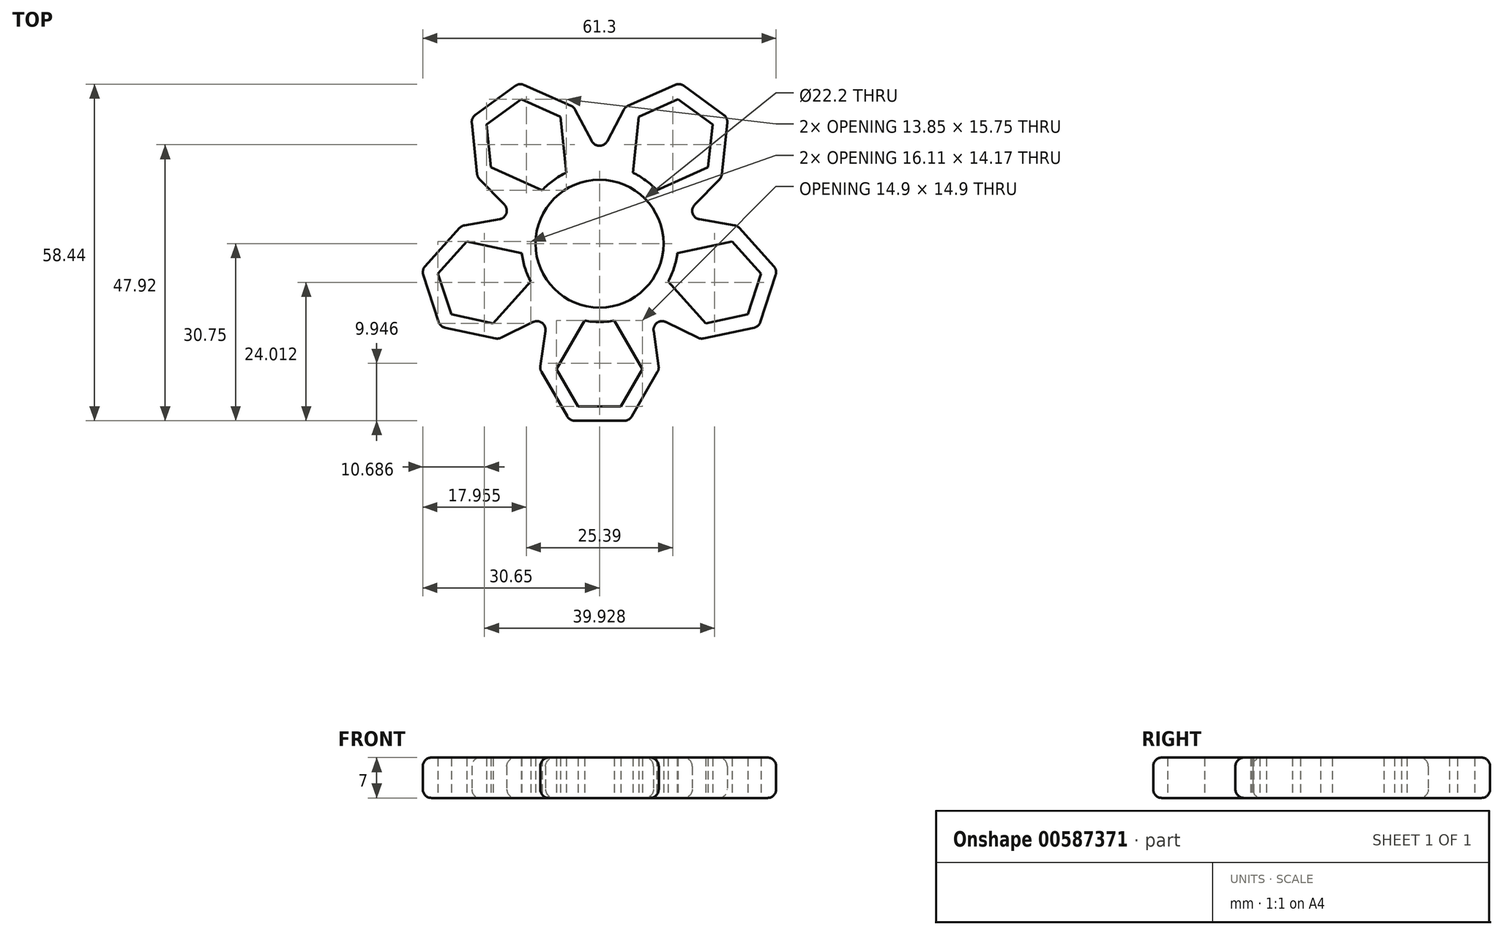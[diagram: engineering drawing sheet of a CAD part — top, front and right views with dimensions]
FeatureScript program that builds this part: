
annotation { "Feature Type Name" : "Feature", "Feature Type Description" : "" }
export const myFeature = defineFeature(function(context is Context, id is Id, definition is map)
    precondition{}
    {
        {
            var Q0;
            Q0=qCreatedBy(makeId("Top.planeOp"),FACE);
            var sketch = newSketch(context, id + "F0", { "sketchPlane" : qUnion([Q0])});
            skCircle(sketch, "E0", {"center": v(0, 0) * mm, "radius": 11.1 * mm});
            skCircle(sketch, "E1.0", {"center": v(0, 0) * mm, "radius": 13.6 * mm});
            skCircle(sketch, "E2.cCircle", {"center": v(0, -21.8) * mm, "radius": 6.45 * mm, "construction": true});
            skLineSegment(sketch, "E2.0", {"start": v(3.72, -28.25) * mm, "end": v(-3.72, -28.25) * mm});
            skLineSegment(sketch, "E2.1", {"start": v(-3.72, -28.25) * mm, "end": v(-7.45, -21.8) * mm});
            skLineSegment(sketch, "E2.2", {"start": v(-7.45, -21.8) * mm, "end": v(-2.96, -14.04) * mm});
            skLineSegment(sketch, "E2.4", {"start": v(3.72, -15.35) * mm, "end": v(7.45, -21.8) * mm});
            skLineSegment(sketch, "E2.5", {"start": v(7.45, -21.8) * mm, "end": v(3.72, -28.25) * mm});
            skPoint(sketch, "E2.0.midPoint", {"position": v(0, -28.25) * mm});
            skLineSegment(sketch, "E3.2", {"start": v(10.33, -21.8) * mm, "end": v(5.17, -30.75) * mm});
            skLineSegment(sketch, "E3.3", {"start": v(5.17, -30.75) * mm, "end": v(-5.17, -30.75) * mm});
            skLineSegment(sketch, "E3.4", {"start": v(-5.17, -30.75) * mm, "end": v(-10.33, -21.8) * mm});
            skLineSegment(sketch, "E4", {"start": v(-10.33, -21.8) * mm, "end": v(-8.7, -10.45) * mm});
            skLineSegment(sketch, "E5", {"start": v(10.33, -21.8) * mm, "end": v(8.7, -10.45) * mm});
            skFitSpline(sketch, "E6", {"points": [v(-8.7, -10.45) * mm, v(8.7, -10.45) * mm], "startDerivative": vector(17.15, -3.94) * mm, "endDerivative": vector(17.1, 4.44) * mm});
            skLineSegment(sketch, "E7", {"start": v(-2.96, -14.04) * mm, "end": v(-2.57, -13.35) * mm});
            skLineSegment(sketch, "E8", {"start": v(3.72, -15.35) * mm, "end": v(2.57, -13.35) * mm});
            skLineSegment(sketch, "E9.1.0", {"start": v(23.93, 3.1) * mm, "end": v(12.63, 5.05) * mm});
            skLineSegment(sketch, "E9.1.1", {"start": v(15.75, -1.2) * mm, "end": v(23.04, 0.35) * mm});
            skLineSegment(sketch, "E9.1.2", {"start": v(23.93, 3.1) * mm, "end": v(30.84, -4.59) * mm});
            skLineSegment(sketch, "E9.1.3", {"start": v(28.02, -5.19) * mm, "end": v(25.72, -12.27) * mm});
            skLineSegment(sketch, "E9.1.4", {"start": v(30.84, -4.59) * mm, "end": v(27.65, -14.42) * mm});
            skPoint(sketch, "E9.1.5", {"position": v(26.87, -8.73) * mm});
            skLineSegment(sketch, "E9.1.6", {"start": v(27.65, -14.42) * mm, "end": v(17.54, -16.57) * mm});
            skLineSegment(sketch, "E9.1.7", {"start": v(17.54, -16.57) * mm, "end": v(7.25, -11.5) * mm});
            skLineSegment(sketch, "E9.1.8", {"start": v(25.72, -12.27) * mm, "end": v(18.43, -13.82) * mm});
            skLineSegment(sketch, "E9.1.9", {"start": v(23.04, 0.35) * mm, "end": v(28.02, -5.19) * mm});
            skLineSegment(sketch, "E9.1.10", {"start": v(15.75, -1.2) * mm, "end": v(13.5, -1.68) * mm});
            skLineSegment(sketch, "E9.1.11", {"start": v(18.43, -13.82) * mm, "end": v(12.43, -7.16) * mm});
            skCircle(sketch, "E9.1.12", {"center": v(20.74, -6.74) * mm, "radius": 6.45 * mm, "construction": true});
            skLineSegment(sketch, "E9.1.13", {"start": v(12.43, -7.16) * mm, "end": v(11.9, -6.57) * mm});
            skLineSegment(sketch, "E9.2.0", {"start": v(4.45, 23.71) * mm, "end": v(-0.9, 13.57) * mm});
            skLineSegment(sketch, "E9.2.1", {"start": v(6.01, 14.6) * mm, "end": v(6.8, 22.02) * mm});
            skLineSegment(sketch, "E9.2.2", {"start": v(4.45, 23.71) * mm, "end": v(13.9, 27.92) * mm});
            skLineSegment(sketch, "E9.2.3", {"start": v(13.6, 25.05) * mm, "end": v(19.62, 20.67) * mm});
            skLineSegment(sketch, "E9.2.4", {"start": v(13.9, 27.92) * mm, "end": v(22.26, 21.84) * mm});
            skPoint(sketch, "E9.2.5", {"position": v(16.6, 22.86) * mm});
            skLineSegment(sketch, "E9.2.6", {"start": v(22.26, 21.84) * mm, "end": v(21.18, 11.56) * mm});
            skLineSegment(sketch, "E9.2.7", {"start": v(21.18, 11.56) * mm, "end": v(13.18, 3.34) * mm});
            skLineSegment(sketch, "E9.2.8", {"start": v(19.62, 20.67) * mm, "end": v(18.84, 13.26) * mm});
            skLineSegment(sketch, "E9.2.9", {"start": v(6.8, 22.02) * mm, "end": v(13.6, 25.05) * mm});
            skLineSegment(sketch, "E9.2.10", {"start": v(6.01, 14.6) * mm, "end": v(5.77, 12.32) * mm});
            skLineSegment(sketch, "E9.2.11", {"start": v(18.84, 13.26) * mm, "end": v(10.65, 9.61) * mm});
            skCircle(sketch, "E9.2.12", {"center": v(12.82, 17.64) * mm, "radius": 6.45 * mm, "construction": true});
            skLineSegment(sketch, "E9.2.13", {"start": v(10.65, 9.61) * mm, "end": v(9.93, 9.3) * mm});
            skLineSegment(sketch, "E9.3.0", {"start": v(-21.18, 11.56) * mm, "end": v(-13.19, 3.33) * mm});
            skLineSegment(sketch, "E9.3.1", {"start": v(-12.04, 10.23) * mm, "end": v(-18.84, 13.26) * mm});
            skLineSegment(sketch, "E9.3.2", {"start": v(-21.18, 11.56) * mm, "end": v(-22.26, 21.84) * mm});
            skLineSegment(sketch, "E9.3.3", {"start": v(-19.62, 20.67) * mm, "end": v(-13.6, 25.05) * mm});
            skLineSegment(sketch, "E9.3.4", {"start": v(-22.26, 21.84) * mm, "end": v(-13.9, 27.92) * mm});
            skPoint(sketch, "E9.3.5", {"position": v(-16.6, 22.86) * mm});
            skLineSegment(sketch, "E9.3.6", {"start": v(-13.9, 27.92) * mm, "end": v(-4.45, 23.71) * mm});
            skLineSegment(sketch, "E9.3.7", {"start": v(-4.45, 23.71) * mm, "end": v(0.9, 13.57) * mm});
            skLineSegment(sketch, "E9.3.8", {"start": v(-13.6, 25.05) * mm, "end": v(-6.8, 22.02) * mm});
            skLineSegment(sketch, "E9.3.9", {"start": v(-18.84, 13.26) * mm, "end": v(-19.62, 20.67) * mm});
            skLineSegment(sketch, "E9.3.10", {"start": v(-12.04, 10.23) * mm, "end": v(-9.93, 9.3) * mm});
            skLineSegment(sketch, "E9.3.11", {"start": v(-6.8, 22.02) * mm, "end": v(-5.85, 13.1) * mm});
            skCircle(sketch, "E9.3.12", {"center": v(-12.82, 17.64) * mm, "radius": 6.45 * mm, "construction": true});
            skLineSegment(sketch, "E9.3.13", {"start": v(-5.85, 13.1) * mm, "end": v(-5.77, 12.32) * mm});
            skLineSegment(sketch, "E9.4.0", {"start": v(-17.54, -16.57) * mm, "end": v(-7.24, -11.51) * mm});
            skLineSegment(sketch, "E9.4.1", {"start": v(-13.45, -8.29) * mm, "end": v(-18.43, -13.82) * mm});
            skLineSegment(sketch, "E9.4.2", {"start": v(-17.54, -16.57) * mm, "end": v(-27.65, -14.42) * mm});
            skLineSegment(sketch, "E9.4.3", {"start": v(-25.72, -12.27) * mm, "end": v(-28.02, -5.19) * mm});
            skLineSegment(sketch, "E9.4.4", {"start": v(-27.65, -14.42) * mm, "end": v(-30.84, -4.59) * mm});
            skPoint(sketch, "E9.4.5", {"position": v(-26.87, -8.73) * mm});
            skLineSegment(sketch, "E9.4.6", {"start": v(-30.84, -4.59) * mm, "end": v(-23.93, 3.1) * mm});
            skLineSegment(sketch, "E9.4.7", {"start": v(-23.93, 3.1) * mm, "end": v(-12.62, 5.05) * mm});
            skLineSegment(sketch, "E9.4.8", {"start": v(-28.02, -5.19) * mm, "end": v(-23.04, 0.35) * mm});
            skLineSegment(sketch, "E9.4.9", {"start": v(-18.43, -13.82) * mm, "end": v(-25.72, -12.27) * mm});
            skLineSegment(sketch, "E9.4.10", {"start": v(-13.45, -8.29) * mm, "end": v(-11.9, -6.57) * mm});
            skLineSegment(sketch, "E9.4.11", {"start": v(-23.04, 0.35) * mm, "end": v(-14.27, -1.52) * mm});
            skCircle(sketch, "E9.4.12", {"center": v(-20.74, -6.74) * mm, "radius": 6.45 * mm, "construction": true});
            skLineSegment(sketch, "E9.4.13", {"start": v(-14.27, -1.52) * mm, "end": v(-13.5, -1.68) * mm});
            skSolve(sketch);
        }
        {
            var Q0;
            Q0=makeQuery(id+"F0.imprint","IMPRINT",FACE,{"disambiguationData":[TD([[makeQuery(id+"F0.imprint","IMPRINT",EDGE,{"derivedFrom":sQuery(id+"F0.wireOp",EDGE,"E0")}),-1.0]])]});
            var Q1;
            {var subQ4=sQuery(id+"F0.wireOp",EDGE,"E6");Q1=makeQuery(id+"F0.imprint","IMPRINT",FACE,{"disambiguationData":[TD([[makeQuery(id+"F0.imprint","IMPRINT",EDGE,{"derivedFrom":subQ4}),-1.0]])]});}
            extrude(context, id + "F1", {"entities" : qUnion([Q0, Q1]), "endBound" : BoundingType.SYMMETRIC, "depth" : 7 * mm, "offsetDistance" : 25 * mm});
        }
        {
            var Q0;
            Q0=makeQuery(id+"F0.imprint","IMPRINT",FACE,{"disambiguationData":[TD([[makeQuery(id+"F0.imprint","IMPRINT",EDGE,{"derivedFrom":sQuery(id+"F0.wireOp",EDGE,"E2.0")}),1.0]])]});
            var Q1;
            {var subQ4=sQuery(id+"F0.wireOp",EDGE,"E6");Q1=makeQuery(id+"F0.imprint","IMPRINT",FACE,{"disambiguationData":[TD([[makeQuery(id+"F0.imprint","IMPRINT",EDGE,{"derivedFrom":subQ4}),-1.0]])]});}
            var Q2;
            {var subQ0=sQuery(id+"F0.wireOp",EDGE,"E9.4.0");var subQ1=sQuery(id+"F0.wireOp",EDGE,"E1.0");var subQ2=makeQuery(id+"F0.imprint","INTERSECT",VERTEX,{"derivedFrom":[subQ1,subQ0]});Q2=makeQuery(id+"F0.imprint","IMPRINT",FACE,{"disambiguationData":[TD([[makeQuery(id+"F0.imprint","IMPRINT",EDGE,{"disambiguationData":[TD([[subQ2,1.0]])],"derivedFrom":subQ1}),-1.0]])]});}
            var Q3;
            Q3=makeQuery(id+"F0.imprint","IMPRINT",FACE,{"disambiguationData":[TD([[makeQuery(id+"F0.imprint","IMPRINT",EDGE,{"derivedFrom":sQuery(id+"F0.wireOp",EDGE,"E9.4.1")}),1.0]])]});
            var Q4;
            {var subQ0=sQuery(id+"F0.wireOp",EDGE,"E9.3.0");var subQ1=sQuery(id+"F0.wireOp",EDGE,"E1.0");var subQ2=makeQuery(id+"F0.imprint","INTERSECT",VERTEX,{"derivedFrom":[subQ1,subQ0]});Q4=makeQuery(id+"F0.imprint","IMPRINT",FACE,{"disambiguationData":[TD([[makeQuery(id+"F0.imprint","IMPRINT",EDGE,{"disambiguationData":[TD([[subQ2,1.0]])],"derivedFrom":subQ1}),-1.0]])]});}
            var Q5;
            Q5=makeQuery(id+"F0.imprint","IMPRINT",FACE,{"disambiguationData":[TD([[makeQuery(id+"F0.imprint","IMPRINT",EDGE,{"derivedFrom":sQuery(id+"F0.wireOp",EDGE,"E9.3.1")}),1.0]])]});
            var Q6;
            {var subQ0=sQuery(id+"F0.wireOp",EDGE,"E9.1.0");var subQ1=sQuery(id+"F0.wireOp",EDGE,"E1.0");var subQ2=makeQuery(id+"F0.imprint","INTERSECT",VERTEX,{"derivedFrom":[subQ1,subQ0]});Q6=makeQuery(id+"F0.imprint","IMPRINT",FACE,{"disambiguationData":[TD([[makeQuery(id+"F0.imprint","IMPRINT",EDGE,{"disambiguationData":[TD([[subQ2,1.0]])],"derivedFrom":subQ1}),-1.0]])]});}
            var Q7;
            Q7=makeQuery(id+"F0.imprint","IMPRINT",FACE,{"disambiguationData":[TD([[makeQuery(id+"F0.imprint","IMPRINT",EDGE,{"derivedFrom":sQuery(id+"F0.wireOp",EDGE,"E9.1.1")}),1.0]])]});
            var Q8;
            {var subQ1=sQuery(id+"F0.wireOp",EDGE,"E1.0");var subQ3=sQuery(id+"F0.wireOp",EDGE,"E9.1.7");var subQ4=makeQuery(id+"F0.imprint","INTERSECT",VERTEX,{"derivedFrom":[subQ1,subQ3]});Q8=makeQuery(id+"F0.imprint","IMPRINT",FACE,{"disambiguationData":[TD([[makeQuery(id+"F0.imprint","IMPRINT",EDGE,{"disambiguationData":[TD([[subQ4,1.0]])],"derivedFrom":subQ3}),-1.0]])]});}
            var Q9;
            Q9=makeQuery(id+"F0.imprint","IMPRINT",FACE,{"disambiguationData":[TD([[makeQuery(id+"F0.imprint","IMPRINT",EDGE,{"derivedFrom":sQuery(id+"F0.wireOp",EDGE,"E9.2.1")}),1.0]])]});
            var Q10;
            {var subQ0=sQuery(id+"F0.wireOp",EDGE,"E9.2.0");var subQ1=sQuery(id+"F0.wireOp",EDGE,"E1.0");var subQ2=makeQuery(id+"F0.imprint","INTERSECT",VERTEX,{"derivedFrom":[subQ1,subQ0]});Q10=makeQuery(id+"F0.imprint","IMPRINT",FACE,{"disambiguationData":[TD([[makeQuery(id+"F0.imprint","IMPRINT",EDGE,{"disambiguationData":[TD([[subQ2,1.0]])],"derivedFrom":subQ1}),-1.0]])]});}
            extrude(context, id + "F2", {"entities" : qUnion([Q0, Q1, Q2, Q3, Q4, Q5, Q6, Q7, Q8, Q9, Q10]), "operationType" : NewBodyOperationType.ADD, "endBound" : BoundingType.SYMMETRIC, "depth" : 7 * mm, "offsetDistance" : 25 * mm});
        }
        {
            var Q0;
            Q0=makeQuery(id+"F2.opExtrude","SWEPT_FACE",FACE,{"disambiguationData":[OSD([sQuery(id+"F0.wireOp",EDGE,"E9.3.2")])]});
            var Q1;
            Q1=makeQuery(id+"F2.opExtrude","SWEPT_FACE",FACE,{"disambiguationData":[OSD([sQuery(id+"F0.wireOp",EDGE,"E9.3.0")])]});
            var Q2;
            Q2=makeQuery(id+"F2.opExtrude","SWEPT_FACE",FACE,{"disambiguationData":[OSD([sQuery(id+"F0.wireOp",EDGE,"E9.3.4")])]});
            var Q3;
            Q3=makeQuery(id+"F2.opExtrude","SWEPT_FACE",FACE,{"disambiguationData":[OSD([sQuery(id+"F0.wireOp",EDGE,"E9.4.6")])]});
            var Q4;
            Q4=makeQuery(id+"F2.opExtrude","SWEPT_FACE",FACE,{"disambiguationData":[OSD([sQuery(id+"F0.wireOp",EDGE,"E9.4.7")])]});
            var Q5;
            Q5=makeQuery(id+"F2.opExtrude","SWEPT_FACE",FACE,{"disambiguationData":[OSD([sQuery(id+"F0.wireOp",EDGE,"E9.4.4")])]});
            var Q6;
            Q6=makeQuery(id+"F2.opExtrude","SWEPT_FACE",FACE,{"disambiguationData":[OSD([sQuery(id+"F0.wireOp",EDGE,"E9.4.0")])]});
            var Q7;
            {var subQ0=sQuery(id+"F0.wireOp",EDGE,"E4");Q7=makeQuery(id+"F2.opExtrude","SWEPT_FACE",FACE,{"disambiguationData":[OSD([subQ0]),TDD([makeQuery(id+"F0.imprint","IMPRINT",EDGE,{"disambiguationData":[TD([[makeQuery(id+"F0.imprint","INTERSECT",VERTEX,{"derivedFrom":[sQuery(id+"F0.wireOp",EDGE,"E3.4"),subQ0]}),-1.0]])],"derivedFrom":subQ0})])]});}
            var Q8;
            Q8=makeQuery(id+"F2.opExtrude","SWEPT_FACE",FACE,{"disambiguationData":[OSD([sQuery(id+"F0.wireOp",EDGE,"E9.4.2")])]});
            var Q9;
            Q9=makeQuery(id+"F2.opExtrude","SWEPT_FACE",FACE,{"disambiguationData":[OSD([sQuery(id+"F0.wireOp",EDGE,"E3.4")])]});
            var Q10;
            Q10=makeQuery(id+"F2.opExtrude","SWEPT_FACE",FACE,{"disambiguationData":[OSD([sQuery(id+"F0.wireOp",EDGE,"E3.3")])]});
            var Q11;
            Q11=makeQuery(id+"F2.opExtrude","SWEPT_FACE",FACE,{"disambiguationData":[OSD([sQuery(id+"F0.wireOp",EDGE,"E3.2")])]});
            var Q12;
            Q12=makeQuery(id+"F2.opExtrude","SWEPT_FACE",FACE,{"disambiguationData":[OSD([sQuery(id+"F0.wireOp",EDGE,"E5")])]});
            var Q13;
            Q13=makeQuery(id+"F2.opExtrude","SWEPT_FACE",FACE,{"disambiguationData":[OSD([sQuery(id+"F0.wireOp",EDGE,"E9.1.7")])]});
            var Q14;
            Q14=makeQuery(id+"F2.opExtrude","SWEPT_FACE",FACE,{"disambiguationData":[OSD([sQuery(id+"F0.wireOp",EDGE,"E9.1.6")])]});
            var Q15;
            Q15=makeQuery(id+"F2.opExtrude","SWEPT_FACE",FACE,{"disambiguationData":[OSD([sQuery(id+"F0.wireOp",EDGE,"E9.1.4")])]});
            var Q16;
            Q16=makeQuery(id+"F2.opExtrude","SWEPT_FACE",FACE,{"disambiguationData":[OSD([sQuery(id+"F0.wireOp",EDGE,"E9.1.2")])]});
            var Q17;
            Q17=makeQuery(id+"F2.opExtrude","SWEPT_FACE",FACE,{"disambiguationData":[OSD([sQuery(id+"F0.wireOp",EDGE,"E9.1.0")])]});
            var Q18;
            Q18=makeQuery(id+"F2.opExtrude","SWEPT_FACE",FACE,{"disambiguationData":[OSD([sQuery(id+"F0.wireOp",EDGE,"E9.2.7")])]});
            var Q19;
            Q19=makeQuery(id+"F2.opExtrude","SWEPT_FACE",FACE,{"disambiguationData":[OSD([sQuery(id+"F0.wireOp",EDGE,"E9.2.6")])]});
            var Q20;
            Q20=makeQuery(id+"F2.opExtrude","SWEPT_FACE",FACE,{"disambiguationData":[OSD([sQuery(id+"F0.wireOp",EDGE,"E9.2.4")])]});
            var Q21;
            Q21=makeQuery(id+"F2.opExtrude","SWEPT_FACE",FACE,{"disambiguationData":[OSD([sQuery(id+"F0.wireOp",EDGE,"E9.2.2")])]});
            var Q22;
            Q22=makeQuery(id+"F2.opExtrude","SWEPT_FACE",FACE,{"disambiguationData":[OSD([sQuery(id+"F0.wireOp",EDGE,"E9.2.0")])]});
            var Q23;
            Q23=makeQuery(id+"F2.opExtrude","SWEPT_FACE",FACE,{"disambiguationData":[OSD([sQuery(id+"F0.wireOp",EDGE,"E9.3.7")])]});
            var Q24;
            Q24=makeQuery(id+"F2.opExtrude","SWEPT_FACE",FACE,{"disambiguationData":[OSD([sQuery(id+"F0.wireOp",EDGE,"E9.3.6")])]});
            fillet(context, id + "F3", {"entities" : qUnion([Q0, Q1, Q2, Q3, Q4, Q5, Q6, Q7, Q8, Q9, Q10, Q11, Q12, Q13, Q14, Q15, Q16, Q17, Q18, Q19, Q20, Q21, Q22, Q23, Q24]), "radius" : 1.5 * mm, "allowEdgeOverflow" : false});
        }
    });
